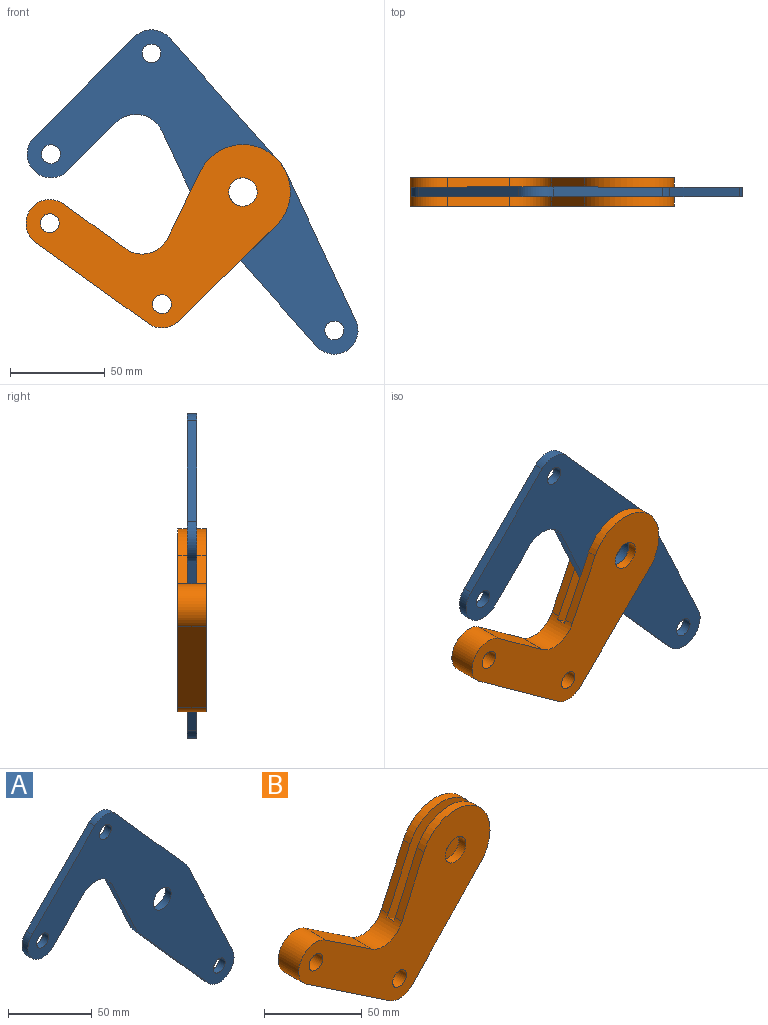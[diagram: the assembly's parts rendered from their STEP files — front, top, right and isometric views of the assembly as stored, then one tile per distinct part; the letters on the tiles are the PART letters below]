
ASSEMBLY  parts=2 mates=1
PART A: 18 faces, bbox 174.4x5x171.1 mm
  f0: cylinder r=25mm len=5.96mm, axis (0,1,0), area 35.8mm2, adj f1,f14,f16,f17
  f1: plane 64.72x57.54mm, normal (0.75,0,0.66), area 433mm2, adj f0,f2,f16,f17
  f2: cylinder r=12.5mm len=18.18mm, axis (0,1,0), area 101.8mm2, adj f1,f3,f16,f17
  f3: plane 53.04x53.03mm, normal (-0.71,0,0.71), area 375mm2, adj f2,f4,f16,f17
  f4: cylinder r=12.5mm len=21.34mm, axis (0,1,0), area 196.3mm2, adj f3,f5,f16,f17
  f5: plane 25.38x25.37mm, normal (0.71,0,-0.71), area 179.4mm2, adj f4,f6,f16,f17
  f6: cylinder r=15mm len=24.18mm, axis (0,1,0), area 143.7mm2, adj f5,f7,f16,f17
  f7: plane 42.96x20.23mm, normal (-0.9,0,-0.43), area 237.4mm2, adj f6,f8,f16,f17
  f8: cylinder r=25mm len=5.96mm, axis (0,1,0), area 35.8mm2, adj f7,f9,f16,f17
  f9: plane 64.72x57.54mm, normal (-0.75,0,-0.66), area 433mm2, adj f8,f10,f16,f17
  f10: cylinder r=12.5mm len=21.84mm, axis (0,1,0), area 178.4mm2, adj f9,f14,f16,f17
  f11: cylinder r=5mm len=10mm, axis (0,1,0), area 157.1mm2, adj f16,f17
  f12: cylinder r=5mm len=10mm, axis (0,1,0), area 157.1mm2, adj f16,f17
  f13: cylinder r=7.5mm len=15mm, axis (0,1,0), area 235.6mm2, adj f16,f17
  f14: plane 78.35x36.89mm, normal (0.9,0,0.43), area 433mm2, adj f0,f10,f16,f17
  f15: cylinder r=5mm len=10mm, axis (0,1,0), area 157.1mm2, adj f16,f17
  f16: plane 174.44x171.05mm, normal (0,-1,0), area 8615mm2, adj f0,f1,f2,f3,f4,f5,f6,f7
  f17: plane 174.44x171.05mm, normal (0,1,0), area 8615mm2, adj f0,f1,f2,f3,f4,f5,f6,f7
PART B: 19 faces, bbox 138.7x15x98.1 mm
  f0: cylinder r=25mm len=47.85mm, axis (0,-1,0), area 435.7mm2, adj f1,f5,f14,f18
  f1: plane 35.82x15.92mm, normal (-0.91,0,0.41), area 196mm2, adj f0,f8,f14,f18
  f2: cylinder r=7.5mm len=15mm, axis (0,-1,0), area 235.6mm2, adj f14,f18
  f3: plane 60.62x40.62mm, normal (-0.56,0,-0.83), area 1094.6mm2, adj f4,f12,f14,f15
  f4: cylinder r=12.5mm len=16mm, axis (0,-1,0), area 262.2mm2, adj f3,f5,f14,f15
  f5: plane 51.99x49.66mm, normal (0.72,0,-0.69), area 871.8mm2, adj f0,f4,f6,f14,f15,f16,f17,f18
  f6: cylinder r=25mm len=47.85mm, axis (0,-1,0), area 435.7mm2, adj f5,f7,f15,f17
  f7: plane 35.82x15.92mm, normal (-0.91,0,0.41), area 196mm2, adj f6,f8,f15,f17
  f8: cylinder r=15mm len=22.06mm, axis (0,-1,0), area 381.6mm2, adj f1,f7,f9,f14,f15,f16,f17,f18
  f9: plane 33.46x22.42mm, normal (0.56,0,0.83), area 604.2mm2, adj f8,f12,f14,f15
  f10: cylinder r=7.5mm len=15mm, axis (0,-1,0), area 235.6mm2, adj f15,f17
  f11: cylinder r=5mm len=15mm, axis (0,-1,0), area 471.2mm2, adj f14,f15
  f12: cylinder r=12.5mm len=22.88mm, axis (0,-1,0), area 589mm2, adj f3,f9,f14,f15
  f13: cylinder r=5mm len=15mm, axis (0,-1,0), area 471.2mm2, adj f14,f15
  f14: plane 138.74x98.12mm, normal (0,1,0), area 5516.2mm2, adj f0,f1,f2,f3,f4,f5,f8,f9
  f15: plane 138.74x98.12mm, normal (0,-1,0), area 5516.2mm2, adj f3,f4,f5,f6,f7,f8,f9,f10
  f16: plane 29.29x19.62mm, normal (0.56,0,0.83), area 176.3mm2, adj f5,f8,f17,f18
  f17: plane 72.15x64.76mm, normal (0,1,0), area 2735.7mm2, adj f5,f6,f7,f8,f10,f16
  f18: plane 72.15x64.76mm, normal (0,-1,0), area 2735.7mm2, adj f0,f1,f2,f5,f8,f16
PLACE A t=(2.39,-2.13,1.71)mm fixed
PLACE B rot(axis=(0,1,0),2deg) t=(2.39,-2.13,1.71)mm
MATE revolute A.f13 <-> B.f2  axis (0,-1,0) through (2.39,2.87,1.71)mm
